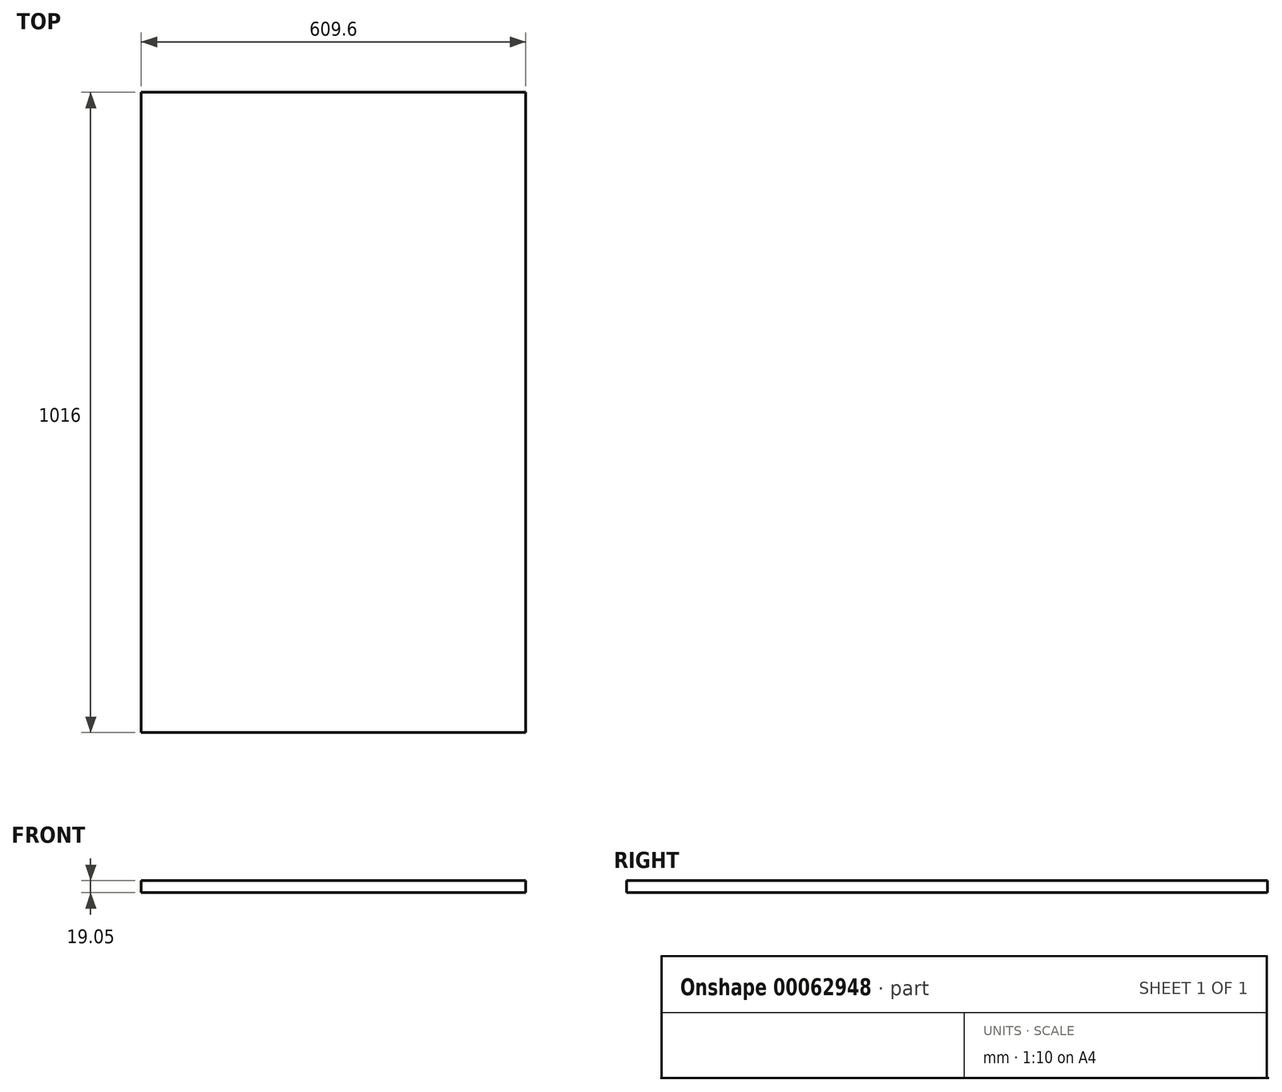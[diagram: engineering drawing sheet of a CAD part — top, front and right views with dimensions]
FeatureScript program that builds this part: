
annotation { "Feature Type Name" : "Feature", "Feature Type Description" : "" }
export const myFeature = defineFeature(function(context is Context, id is Id, definition is map)
    precondition{}
    {
        {
            var Q0;
            Q0=qCreatedBy(makeId("Top.planeOp"),FACE);
            var sketch = newSketch(context, id + "F0", { "sketchPlane" : qUnion([Q0])});
            skLineSegment(sketch, "E0.rect.bottom", {"start": v(304.8, 508) * mm, "end": v(-304.8, 508) * mm});
            skLineSegment(sketch, "E0.rect.top", {"start": v(304.8, -508) * mm, "end": v(-304.8, -508) * mm});
            skLineSegment(sketch, "E0.rect.left", {"start": v(304.8, 508) * mm, "end": v(304.8, -508) * mm});
            skLineSegment(sketch, "E0.rect.right", {"start": v(-304.8, 508) * mm, "end": v(-304.8, -508) * mm});
            skPoint(sketch, "E0.rect.middle", {"position": v(0, 0) * mm});
            skSolve(sketch);
        }
        {
            var Q0;
            Q0 = qSketchRegion(id + "F0", true);
            extrude(context, id + "F1", {"entities" : qUnion([Q0]), "depth" : 19.05 * mm});
        }
    });
